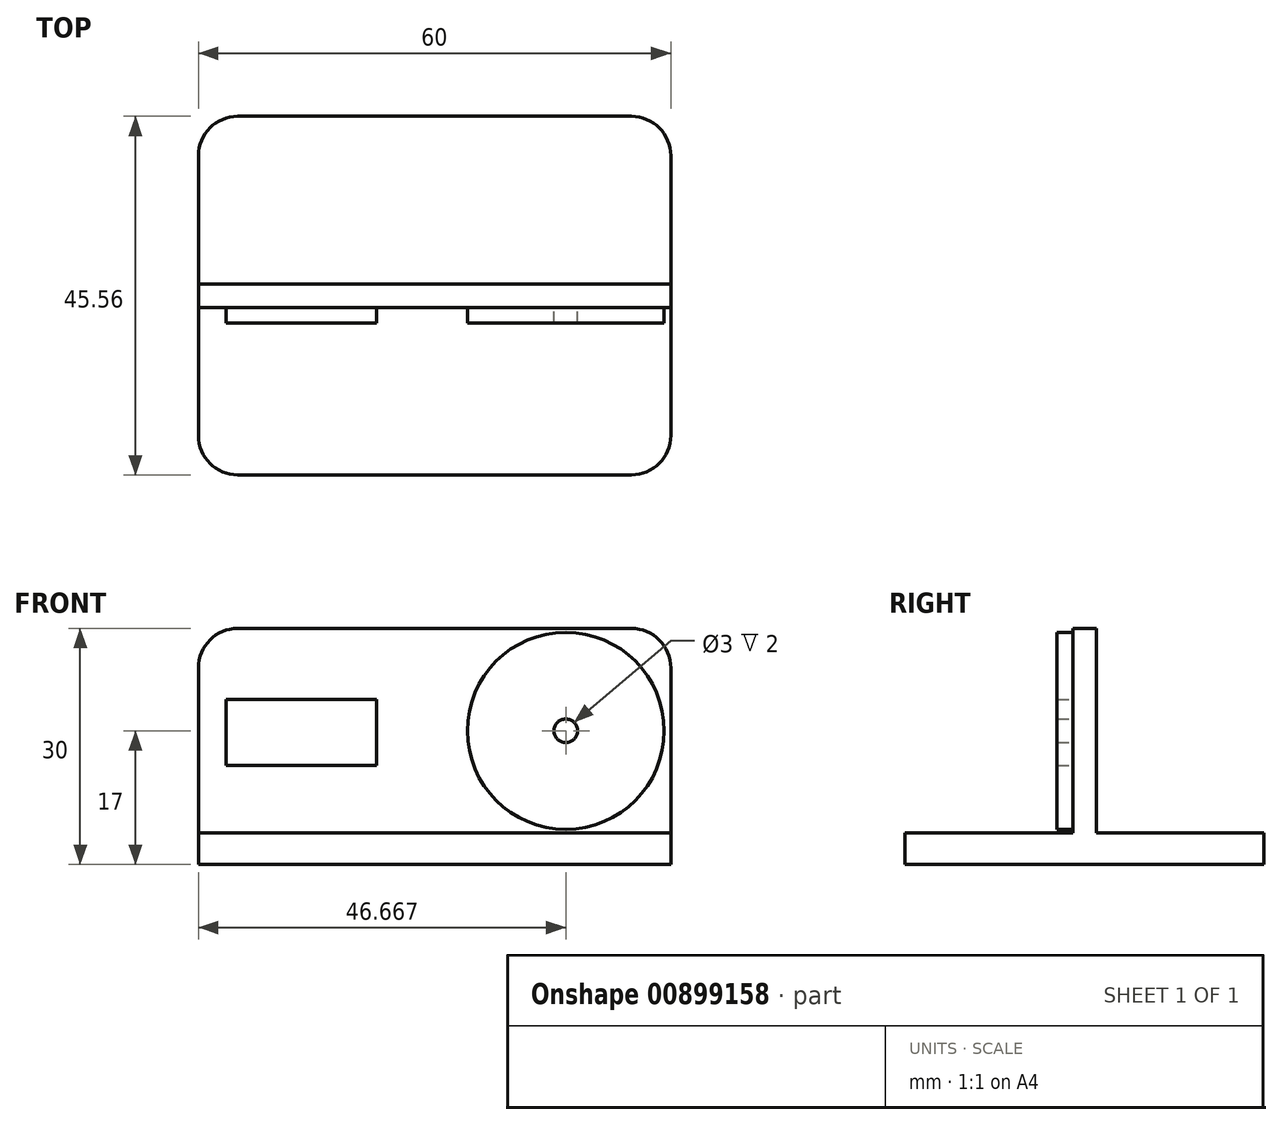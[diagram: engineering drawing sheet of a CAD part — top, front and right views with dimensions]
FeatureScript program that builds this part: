
annotation { "Feature Type Name" : "Feature", "Feature Type Description" : "" }
export const myFeature = defineFeature(function(context is Context, id is Id, definition is map)
    precondition{}
    {
        {
            var Q0;
            Q0=qCreatedBy(makeId("Top.planeOp"),FACE);
            var sketch = newSketch(context, id + "F0", { "sketchPlane" : qUnion([Q0])});
            skLineSegment(sketch, "E0.bottom", {"start": v(30, -22.78) * mm, "end": v(-30, -22.78) * mm});
            skLineSegment(sketch, "E0.top", {"start": v(30, 22.78) * mm, "end": v(-30, 22.78) * mm});
            skLineSegment(sketch, "E0.left", {"start": v(30, -22.78) * mm, "end": v(30, 22.78) * mm});
            skLineSegment(sketch, "E0.right", {"start": v(-30, -22.78) * mm, "end": v(-30, 22.78) * mm});
            skPoint(sketch, "E0.middle", {"position": v(0, 0) * mm});
            skLineSegment(sketch, "E1.bottom", {"start": v(-24.46, -7.9) * mm, "end": v(-3.63, -7.9) * mm, "construction": true});
            skLineSegment(sketch, "E1.top", {"start": v(-24.46, -19.34) * mm, "end": v(-3.63, -19.34) * mm, "construction": true});
            skLineSegment(sketch, "E1.left", {"start": v(-24.46, -7.9) * mm, "end": v(-24.46, -19.34) * mm, "construction": true});
            skLineSegment(sketch, "E1.right", {"start": v(-3.63, -7.9) * mm, "end": v(-3.63, -19.34) * mm, "construction": true});
            skLineSegment(sketch, "E2", {"start": v(0, 0) * mm, "end": v(30, 0) * mm});
            skLineSegment(sketch, "E3", {"start": v(30, 0) * mm, "end": v(-30, 0) * mm});
            skSolve(sketch);
        }
        {
            var Q0;
            Q0=makeQuery(id+"F0.imprint","IMPRINT",FACE,{"disambiguationData":[TD([[makeQuery(id+"F0.imprint","IMPRINT",EDGE,{"derivedFrom":sQuery(id+"F0.wireOp",EDGE,"E0.bottom")}),-1.0]])]});
            var Q1;
            {var subQ1=sQuery(id+"F0.wireOp",EDGE,"E0.top");Q1=makeQuery(id+"F0.imprint","IMPRINT",FACE,{"disambiguationData":[TD([[makeQuery(id+"F0.imprint","IMPRINT",EDGE,{"derivedFrom":subQ1}),1.0]])]});}
            extrude(context, id + "F1", {"entities" : qUnion([Q0, Q1]), "depth" : 4 * mm, "offsetDistance" : 25 * mm});
        }
        {
            var Q0;
            Q0=qCreatedBy(makeId("Front.planeOp"),FACE);
            var sketch = newSketch(context, id + "F2", { "sketchPlane" : qUnion([Q0])});
            skLineSegment(sketch, "E4.bottom", {"start": v(-30, 0) * mm, "end": v(30, 0) * mm});
            skLineSegment(sketch, "E4.top", {"start": v(-30, 30) * mm, "end": v(30, 30) * mm});
            skLineSegment(sketch, "E4.left", {"start": v(-30, 0) * mm, "end": v(-30, 30) * mm});
            skLineSegment(sketch, "E4.right", {"start": v(30, 0) * mm, "end": v(30, 30) * mm});
            skSolve(sketch);
        }
        {
            var Q0;
            Q0=makeQuery(id+"F2.imprint","IMPRINT",FACE,{"disambiguationData":[TD([[makeQuery(id+"F2.imprint","IMPRINT",EDGE,{"derivedFrom":sQuery(id+"F2.wireOp",EDGE,"E4.bottom")}),1.0]])]});
            extrude(context, id + "F3", {"entities" : qUnion([Q0]), "operationType" : NewBodyOperationType.ADD, "depth" : 1.5 * mm, "offsetDistance" : 25 * mm, "hasSecondDirection" : true, "secondDirectionOppositeDirection" : true, "secondDirectionDepth" : 1.5 * mm});
        }
        {
            var Q0;
            Q0=makeQuery(id+"F1.opExtrude","SWEPT_EDGE",EDGE,{"disambiguationData":[OSD([sQuery(id+"F0.wireOp",EDGE,"E0.bottom"),sQuery(id+"F0.wireOp",EDGE,"E0.right")])]});
            var Q1;
            Q1=makeQuery(id+"F1.opExtrude","SWEPT_EDGE",EDGE,{"disambiguationData":[OSD([sQuery(id+"F0.wireOp",EDGE,"E0.bottom"),sQuery(id+"F0.wireOp",EDGE,"E0.left")])]});
            var Q2;
            Q2=makeQuery(id+"F1.opExtrude","SWEPT_EDGE",EDGE,{"disambiguationData":[OSD([sQuery(id+"F0.wireOp",EDGE,"E0.top"),sQuery(id+"F0.wireOp",EDGE,"E0.left")])]});
            var Q3;
            Q3=makeQuery(id+"F1.opExtrude","SWEPT_EDGE",EDGE,{"disambiguationData":[OSD([sQuery(id+"F0.wireOp",EDGE,"E0.top"),sQuery(id+"F0.wireOp",EDGE,"E0.right")])]});
            fillet(context, id + "F4", {"entities" : qUnion([Q0, Q1, Q2, Q3]), "radius" : 5 * mm, "tangentPropagation" : true, "allowEdgeOverflow" : false});
        }
        {
            var Q0;
            Q0=makeQuery(id+"F3.opExtrude","SWEPT_EDGE",EDGE,{"disambiguationData":[OSD([sQuery(id+"F2.wireOp",EDGE,"E4.top"),sQuery(id+"F2.wireOp",EDGE,"E4.left")])]});
            var Q1;
            Q1=makeQuery(id+"F3.opExtrude","SWEPT_EDGE",EDGE,{"disambiguationData":[OSD([sQuery(id+"F2.wireOp",EDGE,"E4.top"),sQuery(id+"F2.wireOp",EDGE,"E4.right")])]});
            fillet(context, id + "F5", {"entities" : qUnion([Q0, Q1]), "radius" : 5 * mm, "tangentPropagation" : true, "allowEdgeOverflow" : false});
        }
        {
            var Q0;
            Q0=makeQuery(id+"F3.opExtrude","CAP_FACE",FACE,{"disambiguationData":[OSD([sQuery(id+"F2.wireOp",EDGE,"E4.bottom"),sQuery(id+"F2.wireOp",EDGE,"E4.top"),sQuery(id+"F2.wireOp",EDGE,"E4.left"),sQuery(id+"F2.wireOp",EDGE,"E4.right")])],"isStart":false});
            var sketch = newSketch(context, id + "F6", { "sketchPlane" : qUnion([Q0])});
            skLineSegment(sketch, "E5.bottom", {"start": v(-26.49, 21) * mm, "end": v(-7.38, 21) * mm});
            skLineSegment(sketch, "E5.top", {"start": v(-26.49, 12.63) * mm, "end": v(-7.38, 12.63) * mm});
            skLineSegment(sketch, "E5.left", {"start": v(-26.49, 21) * mm, "end": v(-26.49, 12.63) * mm});
            skLineSegment(sketch, "E5.right", {"start": v(-7.38, 21) * mm, "end": v(-7.38, 12.63) * mm});
            skCircle(sketch, "E6", {"center": v(16.67, 17) * mm, "radius": 12.5 * mm});
            skCircle(sketch, "E7", {"center": v(16.67, 17) * mm, "radius": 1.5 * mm});
            skSolve(sketch);
        }
        {
            var Q0;
            Q0=makeQuery(id+"F6.imprint","IMPRINT",FACE,{"disambiguationData":[TD([[makeQuery(id+"F6.imprint","IMPRINT",EDGE,{"derivedFrom":sQuery(id+"F6.wireOp",EDGE,"E6")}),1.0]])]});
            var Q1;
            Q1=makeQuery(id+"F6.imprint","IMPRINT",FACE,{"disambiguationData":[TD([[makeQuery(id+"F6.imprint","IMPRINT",EDGE,{"derivedFrom":sQuery(id+"F6.wireOp",EDGE,"E5.bottom")}),-1.0]])]});
            extrude(context, id + "F7", {"entities" : qUnion([Q0, Q1]), "operationType" : NewBodyOperationType.ADD, "depth" : 2 * mm, "offsetDistance" : 25 * mm});
        }
    });
